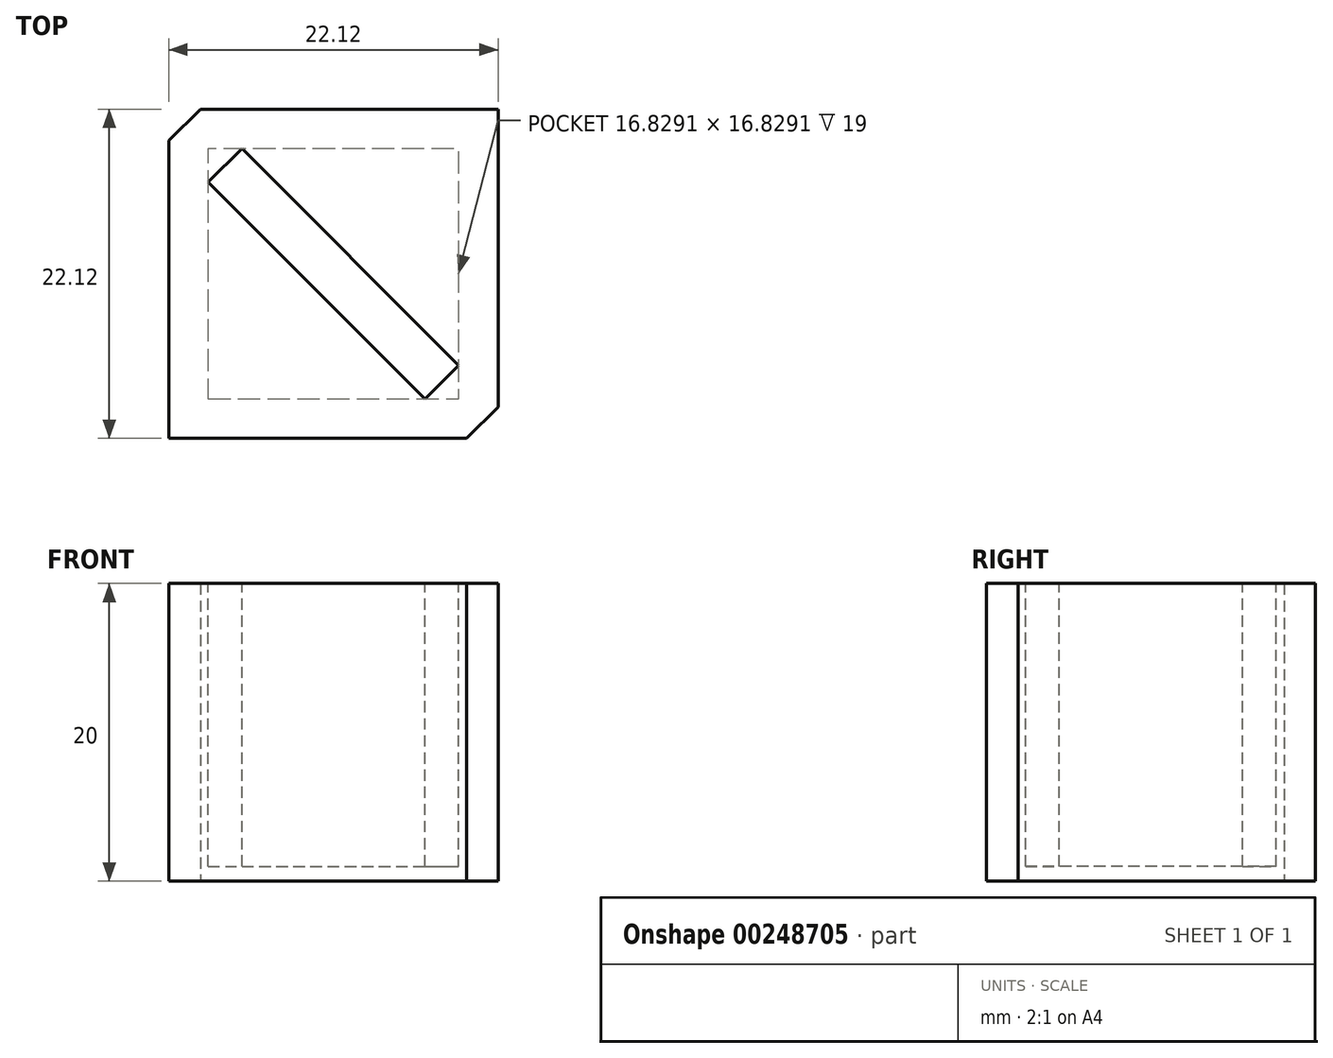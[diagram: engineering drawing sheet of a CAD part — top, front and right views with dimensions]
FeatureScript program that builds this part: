
annotation { "Feature Type Name" : "Feature", "Feature Type Description" : "" }
export const myFeature = defineFeature(function(context is Context, id is Id, definition is map)
    precondition{}
    {
        {
            var Q0;
            Q0=qCreatedBy(makeId("Top.planeOp"),FACE);
            var sketch = newSketch(context, id + "F0", { "sketchPlane" : qUnion([Q0])});
            skLineSegment(sketch, "E0", {"start": v(0, 0) * mm, "end": v(0, 10) * mm});
            skLineSegment(sketch, "E1", {"start": v(0, 10) * mm, "end": v(20, 10) * mm});
            skLineSegment(sketch, "E2", {"start": v(20, 10) * mm, "end": v(20, -10) * mm});
            skLineSegment(sketch, "E3", {"start": v(20, -10) * mm, "end": v(17.88, -12.12) * mm});
            skLineSegment(sketch, "E4", {"start": v(17.88, -12.12) * mm, "end": v(-2.12, -12.12) * mm});
            skLineSegment(sketch, "E5", {"start": v(-2.12, -12.12) * mm, "end": v(-2.12, 7.88) * mm});
            skLineSegment(sketch, "E6", {"start": v(-2.12, 7.88) * mm, "end": v(0, 10) * mm});
            skSolve(sketch);
        }
        {
            var Q0;
            Q0 = qSketchRegion(id + "F0", true);
            extrude(context, id + "F1", {"entities" : qUnion([Q0]), "depth" : 20 * mm});
        }
        {
            var Q0;
            Q0=makeQuery(id+"F1.opExtrude","CAP_FACE",FACE,{"disambiguationData":[OSD([sQuery(id+"F0.wireOp",EDGE,"E1"),sQuery(id+"F0.wireOp",EDGE,"E2"),sQuery(id+"F0.wireOp",EDGE,"E3"),sQuery(id+"F0.wireOp",EDGE,"E4"),sQuery(id+"F0.wireOp",EDGE,"E5"),sQuery(id+"F0.wireOp",EDGE,"E6")])],"isStart":false});
            var sketch = newSketch(context, id + "F2", { "sketchPlane" : qUnion([Q0])});
            skLineSegment(sketch, "E7", {"start": v(-1.06, 8.94) * mm, "end": v(18.94, -11.06) * mm});
            skLineSegment(sketch, "E8.0", {"start": v(-2.2, 7.8) * mm, "end": v(17.8, -12.2) * mm});
            skLineSegment(sketch, "E9.0", {"start": v(0.07, 10.07) * mm, "end": v(20.07, -9.93) * mm});
            skLineSegment(sketch, "E10", {"start": v(0.52, 5.1) * mm, "end": v(2.79, 7.35) * mm});
            skLineSegment(sketch, "E11", {"start": v(15.1, -9.48) * mm, "end": v(17.35, -7.21) * mm});
            skLineSegment(sketch, "E12", {"start": v(8.94, -1.06) * mm, "end": v(10, 0) * mm});
            skSolve(sketch);
        }
        {
            var Q0;
            Q0 = qSketchRegion(id + "F2", true);
            extrude(context, id + "F3", {"entities" : qUnion([Q0]), "operationType" : NewBodyOperationType.REMOVE, "oppositeDirection" : true, "depth" : 19 * mm});
        }
    });
